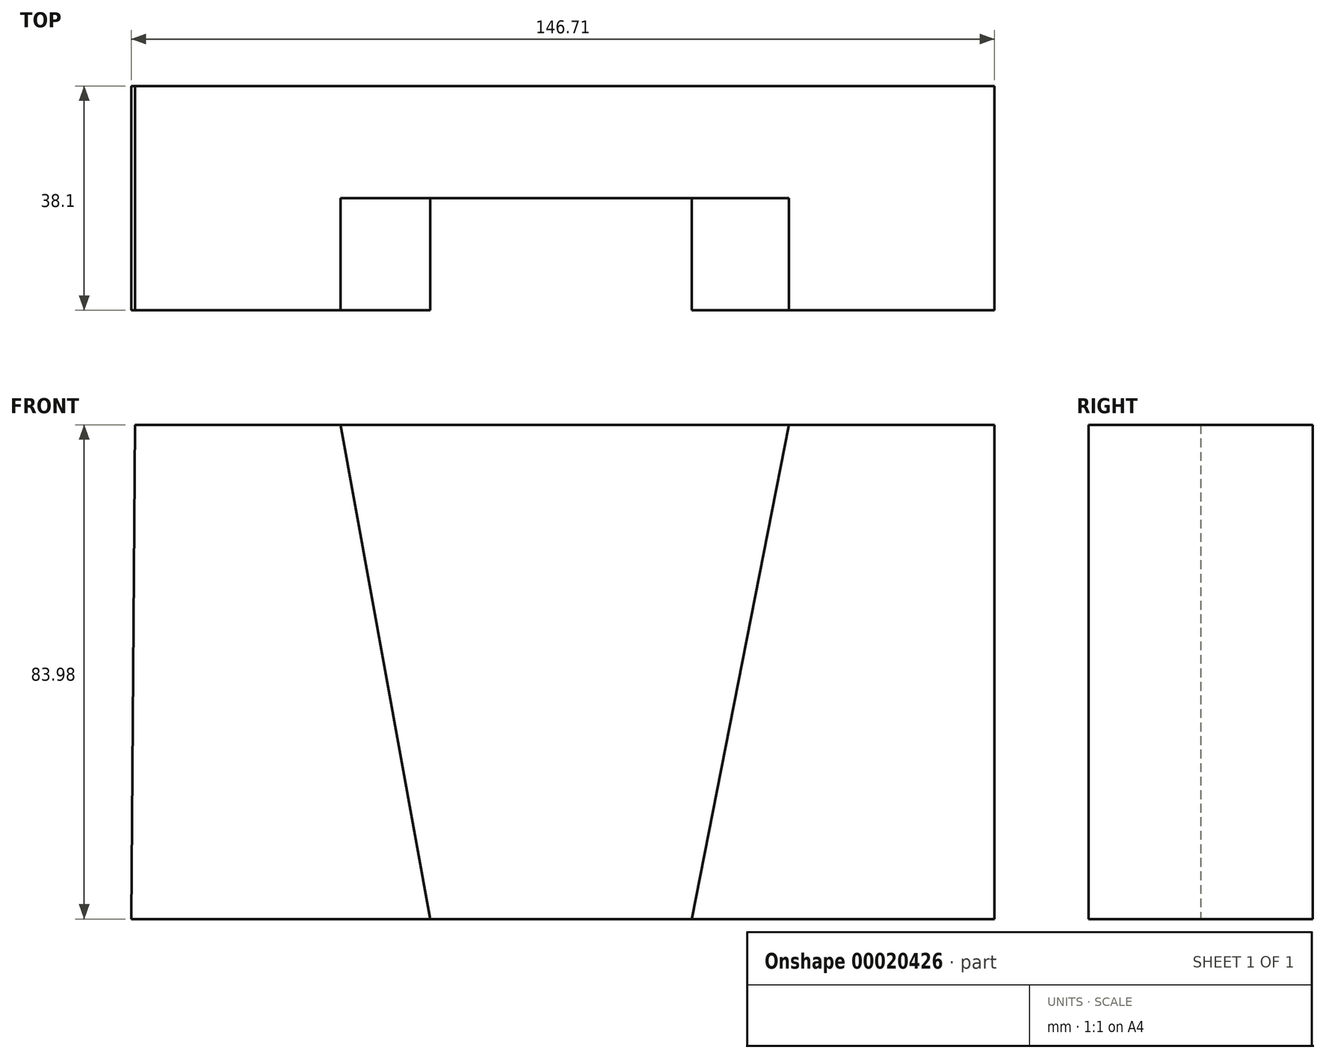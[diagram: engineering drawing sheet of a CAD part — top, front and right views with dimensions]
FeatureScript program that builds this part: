
annotation { "Feature Type Name" : "Feature", "Feature Type Description" : "" }
export const myFeature = defineFeature(function(context is Context, id is Id, definition is map)
    precondition{}
    {
        {
            var Q0;
            Q0=qCreatedBy(makeId("Front.planeOp"),FACE);
            var sketch = newSketch(context, id + "F0", { "sketchPlane" : qUnion([Q0])});
            skLineSegment(sketch, "E0", {"start": v(-71.2, 41.05) * mm, "end": v(74.85, 41.05) * mm});
            skLineSegment(sketch, "E1", {"start": v(74.85, 41.05) * mm, "end": v(74.85, -42.93) * mm});
            skLineSegment(sketch, "E2", {"start": v(74.85, -42.93) * mm, "end": v(-71.86, -42.93) * mm});
            skLineSegment(sketch, "E3", {"start": v(-71.86, -42.93) * mm, "end": v(-71.2, 41.05) * mm});
            skLineSegment(sketch, "E4", {"start": v(-36.27, 41.05) * mm, "end": v(-21.06, -42.93) * mm});
            skLineSegment(sketch, "E5", {"start": v(39.93, 41.05) * mm, "end": v(23.39, -42.93) * mm});
            skSolve(sketch);
        }
        {
            var Q0;
            {var subQ2=sQuery(id+"F0.wireOp",EDGE,"E3");Q0=makeQuery(id+"F0.imprint","IMPRINT",FACE,{"disambiguationData":[TD([[makeQuery(id+"F0.imprint","IMPRINT",EDGE,{"derivedFrom":subQ2}),-1.0]])]});}
            var Q1;
            {var subQ2=sQuery(id+"F0.wireOp",EDGE,"E1");Q1=makeQuery(id+"F0.imprint","IMPRINT",FACE,{"disambiguationData":[TD([[makeQuery(id+"F0.imprint","IMPRINT",EDGE,{"derivedFrom":subQ2}),-1.0]])]});}
            extrude(context, id + "F1", {"entities" : qUnion([Q0, Q1]), "depth" : 38.1 * mm});
        }
        {
            var Q0;
            {var subQ1=sQuery(id+"F0.wireOp",EDGE,"E4");Q0=makeQuery(id+"F0.imprint","IMPRINT",FACE,{"disambiguationData":[TD([[makeQuery(id+"F0.imprint","IMPRINT",EDGE,{"derivedFrom":subQ1}),1.0]])]});}
            extrude(context, id + "F2", {"entities" : qUnion([Q0]), "operationType" : NewBodyOperationType.ADD, "depth" : 19.05 * mm});
        }
    });
